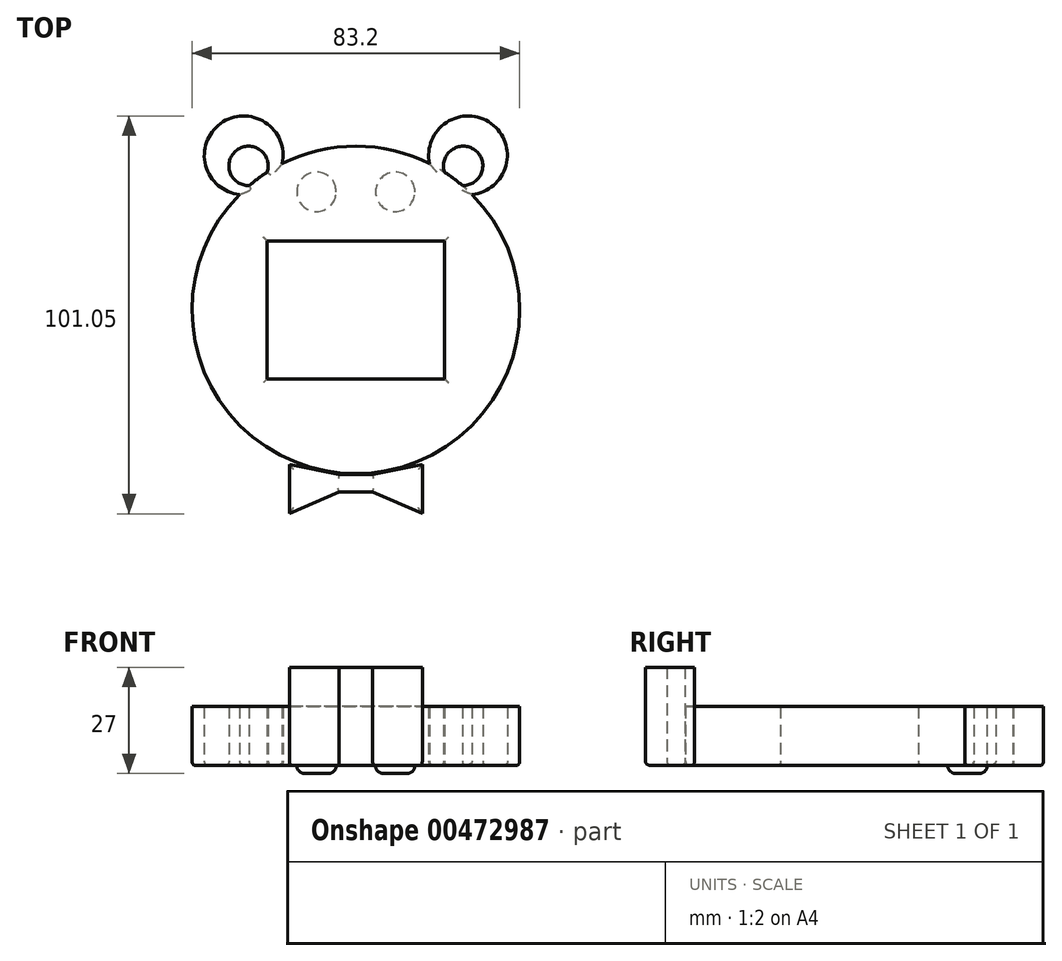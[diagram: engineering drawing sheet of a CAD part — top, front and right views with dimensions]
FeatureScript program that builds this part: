
annotation { "Feature Type Name" : "Feature", "Feature Type Description" : "" }
export const myFeature = defineFeature(function(context is Context, id is Id, definition is map)
    precondition{}
    {
        {
            var Q0;
            Q0=qCreatedBy(makeId("Top.planeOp"),FACE);
            var sketch = newSketch(context, id + "F0", { "sketchPlane" : qUnion([Q0])});
            skLineSegment(sketch, "E0.bottom", {"start": v(22.5, -17.5) * mm, "end": v(-22.5, -17.5) * mm});
            skLineSegment(sketch, "E0.top", {"start": v(22.5, 17.5) * mm, "end": v(-22.5, 17.5) * mm});
            skLineSegment(sketch, "E0.left", {"start": v(22.5, -17.5) * mm, "end": v(22.5, 17.5) * mm});
            skLineSegment(sketch, "E0.right", {"start": v(-22.5, -17.5) * mm, "end": v(-22.5, 17.5) * mm});
            skPoint(sketch, "E0.middle", {"position": v(0, 0) * mm});
            skCircle(sketch, "E1", {"center": v(0, 0) * mm, "radius": 41.6 * mm});
            skArc(sketch, "E2", {"start": v(-18.73, 37.15) * mm, "mid": v(-34.38, 47.36) * mm, "end": v(-29.52, 29.32) * mm});
            skArc(sketch, "E3.MirrorCS", {"start": v(18.73, 37.15) * mm, "mid": v(34.38, 47.36) * mm, "end": v(29.52, 29.32) * mm});
            skArc(sketch, "E4", {"start": v(-22.52, 34.98) * mm, "mid": v(-30.25, 40.59) * mm, "end": v(-27.08, 31.58) * mm});
            skArc(sketch, "E5.MirrorCS", {"start": v(22.52, 34.98) * mm, "mid": v(30.25, 40.59) * mm, "end": v(27.08, 31.58) * mm});
            skSolve(sketch);
        }
        {
            var Q0;
            Q0 = qSketchRegion(id + "F0", true);
            extrude(context, id + "F1", {"entities" : qUnion([Q0]), "depth" : 15 * mm});
        }
        {
            var Q0;
            Q0=qCreatedBy(makeId("Top.planeOp"),FACE);
            var sketch = newSketch(context, id + "F2", { "sketchPlane" : qUnion([Q0])});
            skLineSegment(sketch, "E6.bottom", {"start": v(0, -41.8) * mm, "end": v(4.29, -41.8) * mm});
            skLineSegment(sketch, "E6.top", {"start": v(0, -46.32) * mm, "end": v(4.29, -46.32) * mm});
            skLineSegment(sketch, "E6.left", {"start": v(0, -41.8) * mm, "end": v(0, -46.32) * mm});
            skLineSegment(sketch, "E6.right", {"start": v(4.29, -41.8) * mm, "end": v(4.29, -46.32) * mm});
            skPoint(sketch, "E6.middle", {"position": v(2.14, -44.06) * mm});
            skLineSegment(sketch, "E7", {"start": v(4.29, -41.8) * mm, "end": v(16.87, -39.34) * mm});
            skLineSegment(sketch, "E8", {"start": v(16.87, -39.34) * mm, "end": v(16.87, -51.79) * mm});
            skLineSegment(sketch, "E9", {"start": v(16.87, -51.79) * mm, "end": v(4.29, -46.32) * mm});
            skLineSegment(sketch, "E10.MirrorCS", {"start": v(0, -41.8) * mm, "end": v(-4.29, -41.8) * mm});
            skLineSegment(sketch, "E11.MirrorCS", {"start": v(0, -46.32) * mm, "end": v(-4.29, -46.32) * mm});
            skLineSegment(sketch, "E12.MirrorCS", {"start": v(-4.29, -41.8) * mm, "end": v(-4.29, -46.32) * mm});
            skLineSegment(sketch, "E13.MirrorCS", {"start": v(-4.29, -41.8) * mm, "end": v(-16.87, -39.34) * mm});
            skLineSegment(sketch, "E14.MirrorCS", {"start": v(-16.87, -39.34) * mm, "end": v(-16.87, -51.79) * mm});
            skLineSegment(sketch, "E15.MirrorCS", {"start": v(-16.87, -51.79) * mm, "end": v(-4.29, -46.32) * mm});
            skSolve(sketch);
        }
        {
            var Q0;
            Q0 = qSketchRegion(id + "F2", true);
            extrude(context, id + "F3", {"entities" : qUnion([Q0]), "depth" : 25 * mm});
        }
        {
            var Q0;
            Q0=makeQuery(id+"F1.opExtrude","CAP_FACE",FACE,{"disambiguationData":[OSD([sQuery(id+"F0.wireOp",EDGE,"E0.bottom"),sQuery(id+"F0.wireOp",EDGE,"E0.top"),sQuery(id+"F0.wireOp",EDGE,"E0.left"),sQuery(id+"F0.wireOp",EDGE,"E0.right"),sQuery(id+"F0.wireOp",EDGE,"E1"),sQuery(id+"F0.wireOp",EDGE,"E2"),sQuery(id+"F0.wireOp",EDGE,"E3.MirrorCS"),sQuery(id+"F0.wireOp",EDGE,"E5.MirrorCS"),sQuery(id+"F0.wireOp",EDGE,"E4")])],"isStart":true});
            var sketch = newSketch(context, id + "F4", { "sketchPlane" : qUnion([Q0])});
            skCircle(sketch, "E16", {"center": v(-10, -30) * mm, "radius": 5 * mm});
            skCircle(sketch, "E17", {"center": v(10, -30) * mm, "radius": 5 * mm});
            skSolve(sketch);
        }
        {
            var Q0;
            Q0 = qSketchRegion(id + "F4", true);
            extrude(context, id + "F5", {"entities" : qUnion([Q0]), "depth" : 2 * mm});
        }
        {
            var Q0;
            Q0=makeQuery(id+"F5.opExtrude","CAP_FACE",FACE,{"disambiguationData":[OSD([sQuery(id+"F4.wireOp",EDGE,"E16")])],"isStart":false});
            var Q1;
            Q1=makeQuery(id+"F5.opExtrude","CAP_FACE",FACE,{"disambiguationData":[OSD([sQuery(id+"F4.wireOp",EDGE,"E17")])],"isStart":false});
            fillet(context, id + "F6", {"entities" : qUnion([Q0, Q1]), "radius" : 2 * mm, "tangentPropagation" : true, "allowEdgeOverflow" : false});
        }
        {
            var Q0;
            {var subQ0=sQuery(id+"F0.wireOp",EDGE,"E1");Q0=makeQuery(id+"F1.opExtrude","CAP_EDGE",EDGE,{"disambiguationData":[OSD([subQ0]),TDD([makeQuery(id+"F0.imprint","IMPRINT",EDGE,{"disambiguationData":[TD([[makeQuery(id+"F0.imprint","INTERSECT",VERTEX,{"disambiguationData":[OD(1.0)],"derivedFrom":[subQ0,sQuery(id+"F0.wireOp",EDGE,"E2")]}),-1.0]])],"derivedFrom":subQ0})])],"isStart":true});}
            var Q1;
            Q1=makeQuery(id+"F1.opExtrude","CAP_EDGE",EDGE,{"disambiguationData":[OSD([sQuery(id+"F0.wireOp",EDGE,"E2")])],"isStart":true});
            var Q2;
            {var subQ0=sQuery(id+"F0.wireOp",EDGE,"E1");Q2=makeQuery(id+"F1.opExtrude","CAP_EDGE",EDGE,{"disambiguationData":[OSD([subQ0]),TDD([makeQuery(id+"F0.imprint","IMPRINT",EDGE,{"disambiguationData":[TD([[makeQuery(id+"F0.imprint","INTERSECT",VERTEX,{"disambiguationData":[OD(0.0)],"derivedFrom":[subQ0,sQuery(id+"F0.wireOp",EDGE,"E2")]}),1.0]])],"derivedFrom":subQ0})])],"isStart":true});}
            var Q3;
            Q3=makeQuery(id+"F1.opExtrude","CAP_EDGE",EDGE,{"disambiguationData":[OSD([sQuery(id+"F0.wireOp",EDGE,"E3.MirrorCS")])],"isStart":true});
            var Q4;
            Q4=makeQuery(id+"F1.opExtrude","CAP_EDGE",EDGE,{"disambiguationData":[OSD([sQuery(id+"F0.wireOp",EDGE,"E5.MirrorCS")])],"isStart":true});
            var Q5;
            {var subQ0=sQuery(id+"F0.wireOp",EDGE,"E5.MirrorCS");var subQ1=sQuery(id+"F0.wireOp",EDGE,"E1");Q5=makeQuery(id+"F1.opExtrude","CAP_EDGE",EDGE,{"disambiguationData":[OSD([subQ1]),TDD([makeQuery(id+"F0.imprint","IMPRINT",EDGE,{"disambiguationData":[TD([[makeQuery(id+"F0.imprint","INTERSECT",VERTEX,{"disambiguationData":[OD(0.0)],"derivedFrom":[subQ1,subQ0]}),1.0]])],"derivedFrom":subQ1})])],"isStart":true});}
            var Q6;
            Q6=makeQuery(id+"F1.opExtrude","CAP_EDGE",EDGE,{"disambiguationData":[OSD([sQuery(id+"F0.wireOp",EDGE,"E4")])],"isStart":true});
            var Q7;
            {var subQ0=sQuery(id+"F0.wireOp",EDGE,"E4");var subQ1=sQuery(id+"F0.wireOp",EDGE,"E1");Q7=makeQuery(id+"F1.opExtrude","CAP_EDGE",EDGE,{"disambiguationData":[OSD([subQ1]),TDD([makeQuery(id+"F0.imprint","IMPRINT",EDGE,{"disambiguationData":[TD([[makeQuery(id+"F0.imprint","INTERSECT",VERTEX,{"disambiguationData":[OD(0.0)],"derivedFrom":[subQ1,subQ0]}),-1.0]])],"derivedFrom":subQ1})])],"isStart":true});}
            var Q8;
            Q8=makeQuery(id+"F1.opExtrude","CAP_EDGE",EDGE,{"disambiguationData":[OSD([sQuery(id+"F0.wireOp",EDGE,"E0.bottom")])],"isStart":true});
            var Q9;
            Q9=makeQuery(id+"F1.opExtrude","CAP_EDGE",EDGE,{"disambiguationData":[OSD([sQuery(id+"F0.wireOp",EDGE,"E0.left")])],"isStart":true});
            var Q10;
            Q10=makeQuery(id+"F1.opExtrude","CAP_EDGE",EDGE,{"disambiguationData":[OSD([sQuery(id+"F0.wireOp",EDGE,"E0.top")])],"isStart":true});
            var Q11;
            Q11=makeQuery(id+"F1.opExtrude","CAP_EDGE",EDGE,{"disambiguationData":[OSD([sQuery(id+"F0.wireOp",EDGE,"E0.right")])],"isStart":true});
            fillet(context, id + "F7", {"entities" : qUnion([Q0, Q1, Q2, Q3, Q4, Q5, Q6, Q7, Q8, Q9, Q10, Q11]), "radius" : 1 * mm, "tangentPropagation" : true, "allowEdgeOverflow" : false});
        }
        {
            var Q0;
            Q0=makeQuery(id+"F3.opExtrude","CAP_FACE",FACE,{"disambiguationData":[OSD([sQuery(id+"F2.wireOp",EDGE,"E6.bottom"),sQuery(id+"F2.wireOp",EDGE,"E6.top"),sQuery(id+"F2.wireOp",EDGE,"E7"),sQuery(id+"F2.wireOp",EDGE,"E8"),sQuery(id+"F2.wireOp",EDGE,"E9"),sQuery(id+"F2.wireOp",EDGE,"E10.MirrorCS"),sQuery(id+"F2.wireOp",EDGE,"E11.MirrorCS"),sQuery(id+"F2.wireOp",EDGE,"E13.MirrorCS"),sQuery(id+"F2.wireOp",EDGE,"E14.MirrorCS"),sQuery(id+"F2.wireOp",EDGE,"E15.MirrorCS")])],"isStart":true});
            fillet(context, id + "F8", {"entities" : qUnion([Q0]), "radius" : 1 * mm, "tangentPropagation" : true, "allowEdgeOverflow" : false});
        }
    });
